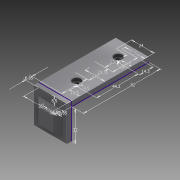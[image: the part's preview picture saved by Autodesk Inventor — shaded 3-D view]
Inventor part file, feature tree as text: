
AUTODESK INVENTOR PART (.ipt)
format: ipt  version: 2015 (Build 190159000, 159)  size: 189,952 bytes
history: native  units: mm
features: fillet x9, extrude x7, sketch x4, chamfer x1
ambient origin geometry x8: Origin, YZ Plane, XZ Plane, XY Plane, X Axis, Y Axis, Z Axis, Center Point
bodies: Solid1 (feature_tree)
feature tree (21):
  sketch  "Sketch1"  dims[d0=35.0mm d1=82.0mm]
  extrude  "Extrusion1"  Depth=82.0mm
  extrude  "Extrusion3"  Depth=24.0mm
  extrude  "Extrusion4"  Depth=26.75mm
  sketch  "Sketch3"  dims[d4=21.0mm d5=26.75mm]
  extrude  "Extrusion5"  Depth=26.0mm
  extrude  "Extrusion6"  Depth=6.85mm
  fillet  "Fillet1"  Radius=5.5mm
  fillet  "Fillet2"  Radius=20.35mm
  fillet  "Fillet3"  Radius=1.5mm
  fillet  "Fillet4"  Radius=4.5mm
  fillet  "Fillet5"  Radius=4.5mm
  fillet  "Fillet6"  Radius=44.2mm
  fillet  "Fillet7"  Radius=10.5mm
  fillet  "Fillet8"  Radius=14.3mm
  fillet  "Fillet9"  Radius=10.5mm
  extrude  "Extrusion7"  Depth=5.0mm TaperAngle=0.0deg
  extrude  "Extrusion8"  Depth=8.5mm
  chamfer  "Chamfer1"  Distance=8.5mm
  sketch  "Sketch2"  dims[d2=21.0mm d3=24.0mm]
  sketch  "Sketch4"  dims[d6=23.1mm d7=26.0mm d8=6.85mm d9=5.5mm d10=20.35mm d11=1.5mm d12=0.0mm d15=4.5mm d16=4.5mm d17=44.2mm d18=10.5mm d19=14.3mm d20=10.5mm d21=5.0mm d22=0.0mm d23=8.5mm d24=8.5mm d25=3.0mm d26=0.0mm d27=32.0mm d28=8.5mm d29=2.85mm d30=18.65mm d31=5.0mm d32=0.0mm d33=1.5mm d34=0.0mm d35=1.0mm d36=1.0mm d37=1.0mm d38=1.0mm d39=1.0mm d40=1.0mm d41=1.0mm d42=1.0mm d43=1.0mm d44=1.5mm d45=0.0mm d46=16.0mm d47=16.0mm d48=9.5mm d49=8.0mm d50=5.0mm d51=0.0mm d52=5.0mm d53=2.0mm d54=45.0deg]
